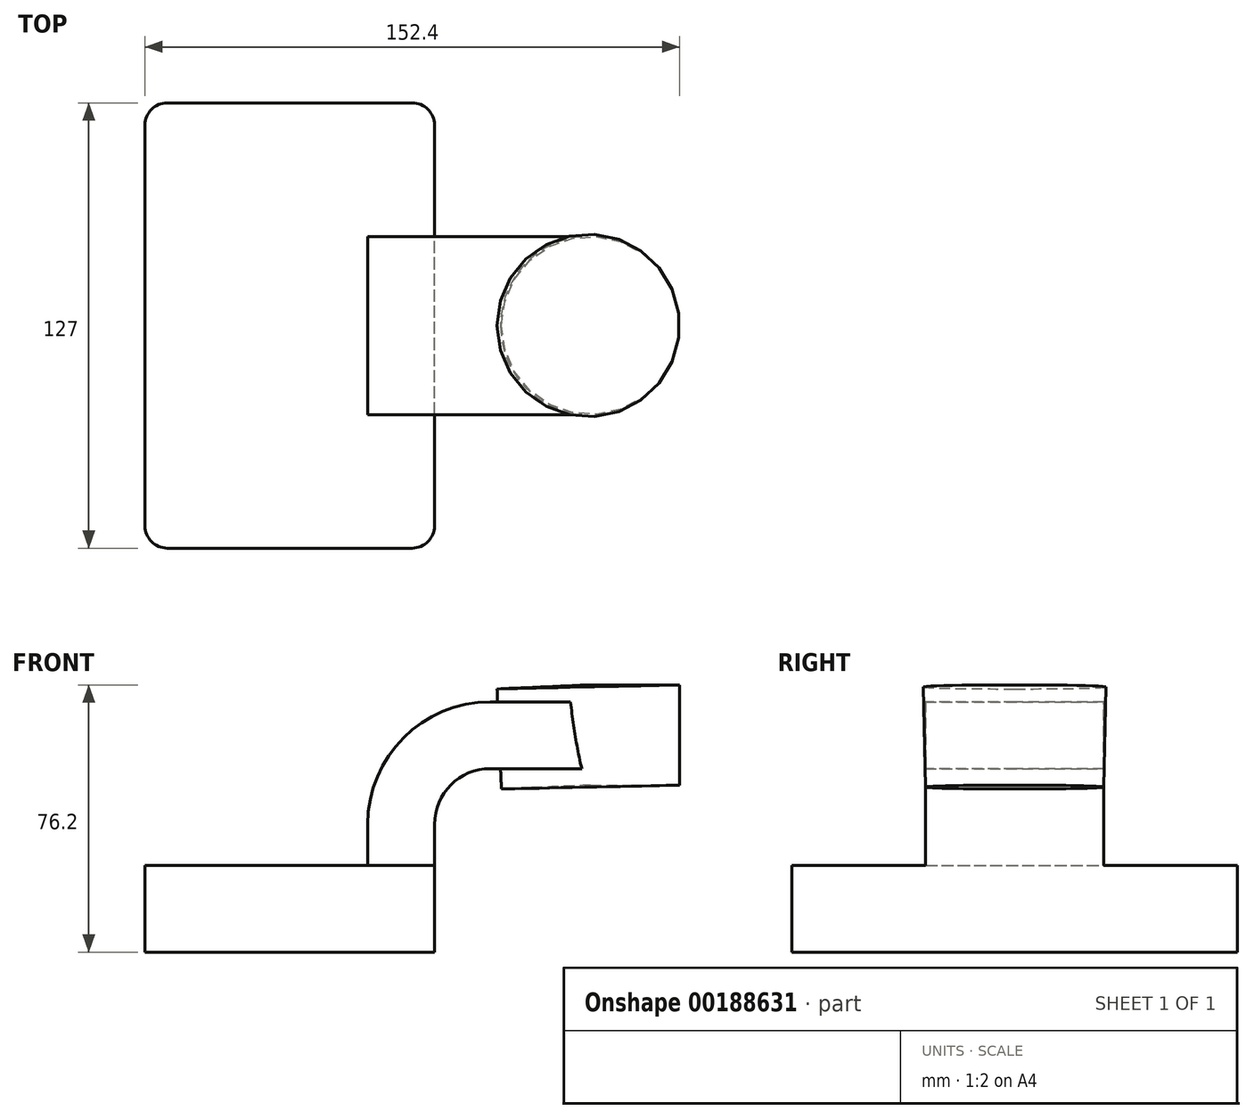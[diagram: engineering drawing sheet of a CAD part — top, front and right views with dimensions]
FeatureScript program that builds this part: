
annotation { "Feature Type Name" : "Feature", "Feature Type Description" : "" }
export const myFeature = defineFeature(function(context is Context, id is Id, definition is map)
    precondition{}
    {
        {
            var Q0;
            Q0=qCreatedBy(makeId("Front.planeOp"),FACE);
            var sketch = newSketch(context, id + "F0", { "sketchPlane" : qUnion([Q0])});
            skLineSegment(sketch, "E0.bottom", {"start": v(-41.28, 12.33) * mm, "end": v(41.28, 12.33) * mm});
            skLineSegment(sketch, "E0.top", {"start": v(-41.28, -12.33) * mm, "end": v(41.28, -12.33) * mm});
            skLineSegment(sketch, "E0.left", {"start": v(-41.28, 12.33) * mm, "end": v(-41.28, -12.33) * mm});
            skLineSegment(sketch, "E0.right", {"start": v(41.28, 12.33) * mm, "end": v(41.28, -12.33) * mm});
            skPoint(sketch, "E0.middle", {"position": v(0, 0) * mm});
            skLineSegment(sketch, "E1.bottom", {"start": v(60.32, 63.87) * mm, "end": v(111.12, 63.87) * mm});
            skLineSegment(sketch, "E1.top", {"start": v(60.33, 35.3) * mm, "end": v(111.12, 35.3) * mm});
            skLineSegment(sketch, "E1.left", {"start": v(60.32, 63.87) * mm, "end": v(60.33, 35.3) * mm});
            skLineSegment(sketch, "E1.right", {"start": v(111.12, 63.87) * mm, "end": v(111.12, 35.3) * mm});
            skPoint(sketch, "E1.middle", {"position": v(85.72, 49.58) * mm});
            skLineSegment(sketch, "E2", {"start": v(41.28, 12.33) * mm, "end": v(41.28, 24.11) * mm});
            skArc(sketch, "E3", {"start": v(41.27, 24.11) * mm, "mid": v(45.92, 35.34) * mm, "end": v(57.15, 39.99) * mm});
            skLineSegment(sketch, "E4", {"start": v(57.15, 39.99) * mm, "end": v(85.1, 39.99) * mm});
            skLineSegment(sketch, "E5.0", {"start": v(57.15, 59.04) * mm, "end": v(85.1, 59.04) * mm});
            skArc(sketch, "E5.1", {"start": v(22.23, 24.11) * mm, "mid": v(32.45, 48.8) * mm, "end": v(57.15, 59.04) * mm});
            skLineSegment(sketch, "E5.2", {"start": v(22.22, 12.33) * mm, "end": v(22.22, 24.11) * mm});
            skLineSegment(sketch, "E6", {"start": v(85.72, 35.3) * mm, "end": v(85.1, 63.87) * mm});
            skFitSpline(sketch, "E7", {"points": [v(-41.28, 12.33) * mm, v(57.15, 59.04) * mm], "startDerivative": vector(26, 116.26) * mm, "endDerivative": vector(106.98, -21.74) * mm});
            skLineSegment(sketch, "E8", {"start": v(85.1, 39.99) * mm, "end": v(85.1, 59.04) * mm});
            skSolve(sketch);
        }
        {
            var Q0;
            Q0=makeQuery(id+"F0.imprint","IMPRINT",FACE,{"disambiguationData":[TD([[makeQuery(id+"F0.imprint","IMPRINT",EDGE,{"derivedFrom":sQuery(id+"F0.wireOp",EDGE,"E0.top")}),1.0]])]});
            extrude(context, id + "F1", {"entities" : qUnion([Q0]), "endBound" : BoundingType.SYMMETRIC, "depth" : 127 * mm});
        }
        {
            var Q0;
            {var subQ1=sQuery(id+"F0.wireOp",EDGE,"E2");Q0=makeQuery(id+"F0.imprint","IMPRINT",FACE,{"disambiguationData":[TD([[makeQuery(id+"F0.imprint","IMPRINT",EDGE,{"derivedFrom":subQ1}),1.0]])]});}
            var Q1;
            {var subQ5=sQuery(id+"F0.wireOp",EDGE,"E8");Q1=makeQuery(id+"F0.imprint","IMPRINT",FACE,{"disambiguationData":[TD([[makeQuery(id+"F0.imprint","IMPRINT",EDGE,{"derivedFrom":subQ5}),1.0]])]});}
            extrude(context, id + "F2", {"entities" : qUnion([Q0, Q1]), "operationType" : NewBodyOperationType.ADD, "endBound" : BoundingType.SYMMETRIC, "depth" : 50.8 * mm});
        }
        {
            var Q0;
            Q0=makeQuery(id+"F0.imprint","IMPRINT",FACE,{"disambiguationData":[TD([[makeQuery(id+"F0.imprint","IMPRINT",EDGE,{"derivedFrom":sQuery(id+"F0.wireOp",EDGE,"E5.1")}),1.0]])]});
            extrude(context, id + "F3", {"entities" : qUnion([Q0]), "operationType" : NewBodyOperationType.ADD, "endBound" : BoundingType.SYMMETRIC, "depth" : 15.88 * mm});
        }
        {
            var Q0;
            {var subQ0=sQuery(id+"F0.wireOp",EDGE,"E1.right");Q0=makeQuery(id+"F0.imprint","IMPRINT",FACE,{"disambiguationData":[TD([[makeQuery(id+"F0.imprint","IMPRINT",EDGE,{"derivedFrom":subQ0}),-1.0]])]});}
            var Q1;
            Q1=sQuery(id+"F0.wireOp",EDGE,"E6");
            revolve(context, id + "F4", {"operationType" : NewBodyOperationType.ADD, "entities" : qUnion([Q0]), "axis" : qUnion([Q1]), "revolveType" : RevolveType.FULL});
        }
        {
            var Q0;
            Q0=makeQuery(id+"F1.opExtrude","CAP_EDGE",EDGE,{"disambiguationData":[OSD([sQuery(id+"F0.wireOp",EDGE,"E0.left")])],"isStart":false});
            var Q1;
            Q1=makeQuery(id+"F1.opExtrude","CAP_EDGE",EDGE,{"disambiguationData":[OSD([sQuery(id+"F0.wireOp",EDGE,"E0.right")])],"isStart":false});
            var Q2;
            Q2=makeQuery(id+"F1.opExtrude","CAP_EDGE",EDGE,{"disambiguationData":[OSD([sQuery(id+"F0.wireOp",EDGE,"E0.right")])],"isStart":true});
            var Q3;
            Q3=makeQuery(id+"F1.opExtrude","CAP_EDGE",EDGE,{"disambiguationData":[OSD([sQuery(id+"F0.wireOp",EDGE,"E0.left")])],"isStart":true});
            fillet(context, id + "F5", {"entities" : qUnion([Q0, Q1, Q2, Q3]), "radius" : 6.35 * mm, "tangentPropagation" : true, "allowEdgeOverflow" : false});
        }
    });
